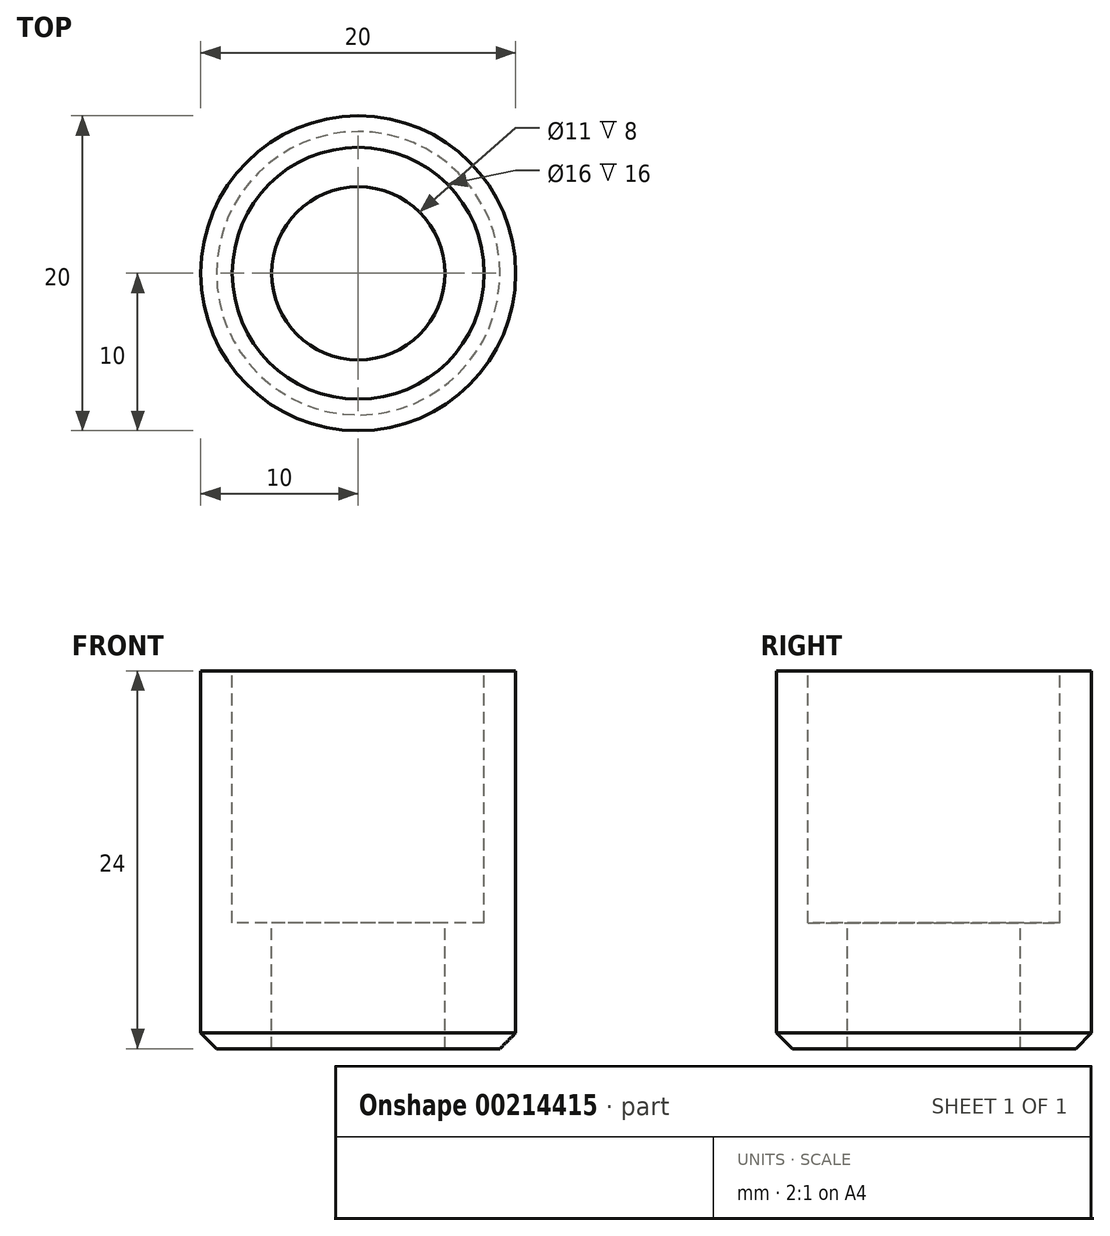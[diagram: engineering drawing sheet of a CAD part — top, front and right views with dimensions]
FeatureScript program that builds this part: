
annotation { "Feature Type Name" : "Feature", "Feature Type Description" : "" }
export const myFeature = defineFeature(function(context is Context, id is Id, definition is map)
    precondition{}
    {
        {
            var Q0;
            Q0=qCreatedBy(makeId("Top.planeOp"),FACE);
            var sketch = newSketch(context, id + "F0", { "sketchPlane" : qUnion([Q0])});
            skCircle(sketch, "E0", {"center": v(0, 0) * mm, "radius": 10 * mm});
            skSolve(sketch);
        }
        {
            var Q0;
            Q0 = qSketchRegion(id + "F0", true);
            extrude(context, id + "F1", {"entities" : qUnion([Q0]), "depth" : 24 * mm});
        }
        {
            var Q0;
            Q0=makeQuery(id+"F1.opExtrude","CAP_EDGE",EDGE,{"disambiguationData":[OSD([sQuery(id+"F0.wireOp",EDGE,"E0")])],"isStart":true});
            chamfer(context, id + "F2", {"entities" : qUnion([Q0]), "width" : 1 * mm, "tangentPropagation" : true});
        }
        {
            var Q0;
            Q0=makeQuery(id+"F1.opExtrude","CAP_FACE",FACE,{"disambiguationData":[OSD([sQuery(id+"F0.wireOp",EDGE,"E0")])],"isStart":false});
            var sketch = newSketch(context, id + "F3", { "sketchPlane" : qUnion([Q0])});
            skCircle(sketch, "E1", {"center": v(0, 0) * mm, "radius": 5.5 * mm});
            skSolve(sketch);
        }
        {
            var Q0;
            Q0 = qSketchRegion(id + "F3", true);
            extrude(context, id + "F4", {"entities" : qUnion([Q0]), "operationType" : NewBodyOperationType.REMOVE, "endBound" : BoundingType.THROUGH_ALL, "oppositeDirection" : true, "depth" : 25 * mm});
        }
        {
            var Q0;
            Q0=makeQuery(id+"F1.opExtrude","CAP_FACE",FACE,{"disambiguationData":[OSD([sQuery(id+"F0.wireOp",EDGE,"E0")])],"isStart":false});
            var sketch = newSketch(context, id + "F5", { "sketchPlane" : qUnion([Q0])});
            skCircle(sketch, "E2", {"center": v(0, 0) * mm, "radius": 8 * mm});
            skSolve(sketch);
        }
        {
            var Q0;
            Q0 = qSketchRegion(id + "F5", true);
            extrude(context, id + "F6", {"entities" : qUnion([Q0]), "operationType" : NewBodyOperationType.REMOVE, "oppositeDirection" : true, "depth" : 16 * mm});
        }
    });
